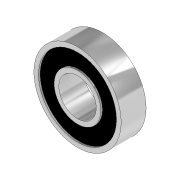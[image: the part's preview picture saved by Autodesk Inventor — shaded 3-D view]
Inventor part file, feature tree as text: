
AUTODESK INVENTOR PART (.ipt)
format: ipt  version: 2020 (Build 240168000, 168)  size: 123,392 bytes
history: native  units: in
note: dims shown in document units (in); Inventor stores cm internally (conversion verified against a paired STEP export)
features: extrude x3, sketch x3, projected_geometry x2
ambient origin geometry x8: Origin, YZ Plane, XZ Plane, XY Plane, X Axis, Y Axis, Z Axis, Center Point
bodies: Solid1 (feature_tree)
feature tree (8):
  extrude  "Extrusion1"  Depth=1.1024in
  extrude  "Extrusion2"  Depth=0.315in
  extrude  "Extrusion3"  Depth=0.0197in TaperAngle=0.0deg
  sketch  "Sketch1"  dims[d0=0.4724in d1=1.1024in]
  sketch  "Sketch2"  dims[d2=0.315in d3=0.0in d4=0.0591in]
  projected_geometry  "Projected Loop1"
  sketch  "Sketch3"  dims[d5=0.0591in d6=0.0197in d7=0.0in d8=0.0197in d9=0.0in]
  projected_geometry  "Projected Loop2"
